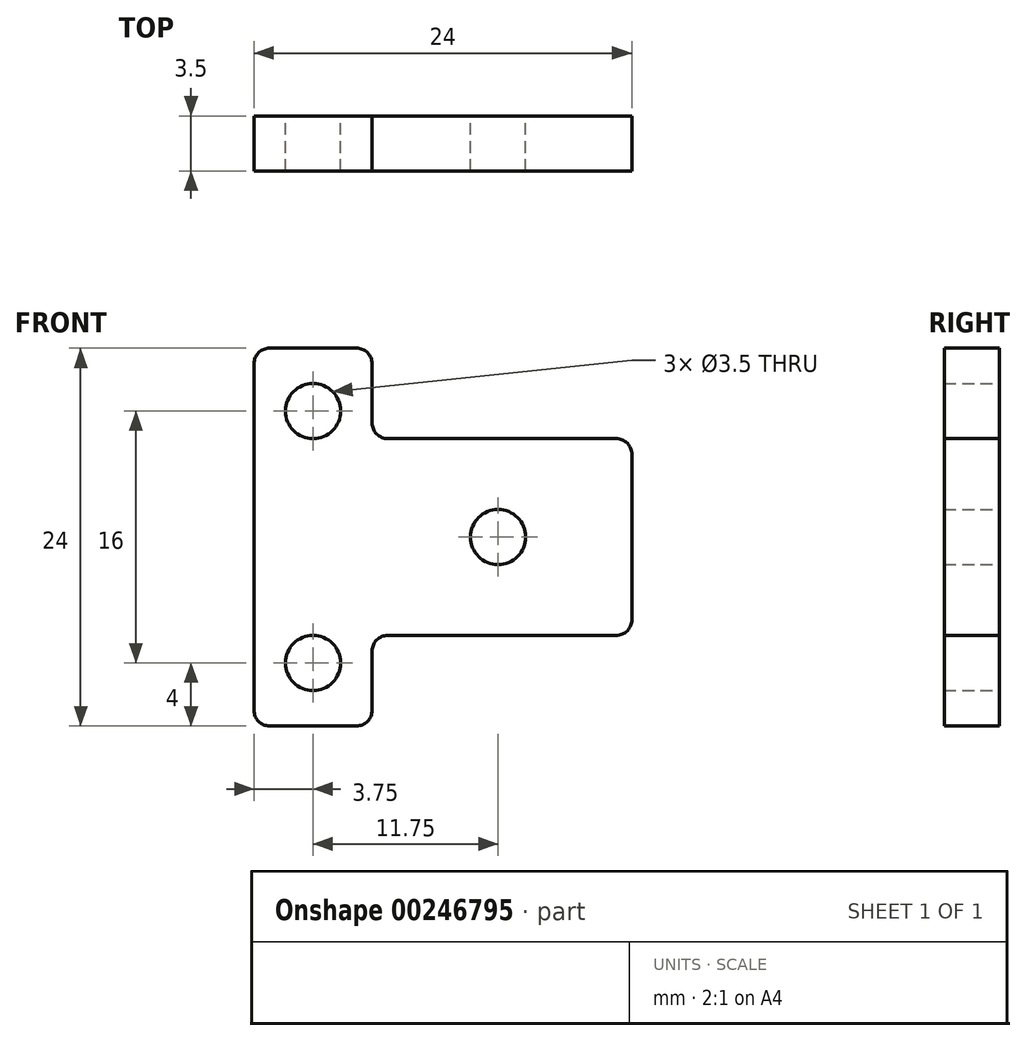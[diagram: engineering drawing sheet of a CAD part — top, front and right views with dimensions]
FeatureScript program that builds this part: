
annotation { "Feature Type Name" : "Feature", "Feature Type Description" : "" }
export const myFeature = defineFeature(function(context is Context, id is Id, definition is map)
    precondition{}
    {
        {
            var Q0;
            Q0=qCreatedBy(makeId("Front.planeOp"),FACE);
            var sketch = newSketch(context, id + "F0", { "sketchPlane" : qUnion([Q0])});
            skLineSegment(sketch, "E0", {"start": v(0, 0) * mm, "end": v(0, 12) * mm});
            skLineSegment(sketch, "E1", {"start": v(0, 12) * mm, "end": v(7.5, 12) * mm});
            skLineSegment(sketch, "E2", {"start": v(7.5, 12) * mm, "end": v(7.5, 6.25) * mm});
            skLineSegment(sketch, "E3", {"start": v(7.5, 6.25) * mm, "end": v(24, 6.25) * mm});
            skLineSegment(sketch, "E4", {"start": v(24, 6.25) * mm, "end": v(24, -6.25) * mm});
            skLineSegment(sketch, "E5", {"start": v(24, -6.25) * mm, "end": v(7.5, -6.25) * mm});
            skLineSegment(sketch, "E6", {"start": v(7.5, -6.25) * mm, "end": v(7.5, -12) * mm});
            skLineSegment(sketch, "E7", {"start": v(7.5, -12) * mm, "end": v(0, -12) * mm});
            skLineSegment(sketch, "E8", {"start": v(0, -12) * mm, "end": v(0, 0) * mm});
            skCircle(sketch, "E9", {"center": v(15.5, 0) * mm, "radius": 1.75 * mm});
            skCircle(sketch, "E10", {"center": v(3.75, 8) * mm, "radius": 1.75 * mm});
            skCircle(sketch, "E11", {"center": v(3.75, -8) * mm, "radius": 1.75 * mm});
            skSolve(sketch);
        }
        {
            var Q0;
            Q0 = qSketchRegion(id + "F0", true);
            extrude(context, id + "F1", {"entities" : qUnion([Q0]), "depth" : 3.5 * mm});
        }
        {
            var Q0;
            Q0=makeQuery(id+"F1.opExtrude","SWEPT_EDGE",EDGE,{"disambiguationData":[OSD([sQuery(id+"F0.wireOp",EDGE,"E6"),sQuery(id+"F0.wireOp",EDGE,"E7")])]});
            var Q1;
            Q1=makeQuery(id+"F1.opExtrude","SWEPT_EDGE",EDGE,{"disambiguationData":[OSD([sQuery(id+"F0.wireOp",EDGE,"E4"),sQuery(id+"F0.wireOp",EDGE,"E5")])]});
            var Q2;
            Q2=makeQuery(id+"F1.opExtrude","SWEPT_EDGE",EDGE,{"disambiguationData":[OSD([sQuery(id+"F0.wireOp",EDGE,"E7"),sQuery(id+"F0.wireOp",EDGE,"E8")])]});
            var Q3;
            Q3=makeQuery(id+"F1.opExtrude","SWEPT_EDGE",EDGE,{"disambiguationData":[OSD([sQuery(id+"F0.wireOp",EDGE,"E3"),sQuery(id+"F0.wireOp",EDGE,"E4")])]});
            var Q4;
            Q4=makeQuery(id+"F1.opExtrude","SWEPT_EDGE",EDGE,{"disambiguationData":[OSD([sQuery(id+"F0.wireOp",EDGE,"E1"),sQuery(id+"F0.wireOp",EDGE,"E2")])]});
            var Q5;
            Q5=makeQuery(id+"F1.opExtrude","SWEPT_EDGE",EDGE,{"disambiguationData":[OSD([sQuery(id+"F0.wireOp",EDGE,"E2"),sQuery(id+"F0.wireOp",EDGE,"E3")])]});
            var Q6;
            Q6=makeQuery(id+"F1.opExtrude","SWEPT_EDGE",EDGE,{"disambiguationData":[OSD([sQuery(id+"F0.wireOp",EDGE,"E0"),sQuery(id+"F0.wireOp",EDGE,"E1")])]});
            var Q7;
            Q7=makeQuery(id+"F1.opExtrude","SWEPT_EDGE",EDGE,{"disambiguationData":[OSD([sQuery(id+"F0.wireOp",EDGE,"E5"),sQuery(id+"F0.wireOp",EDGE,"E6")])]});
            fillet(context, id + "F2", {"entities" : qUnion([Q0, Q1, Q2, Q3, Q4, Q5, Q6, Q7]), "radius" : 1 * mm, "tangentPropagation" : true, "allowEdgeOverflow" : false});
        }
    });
